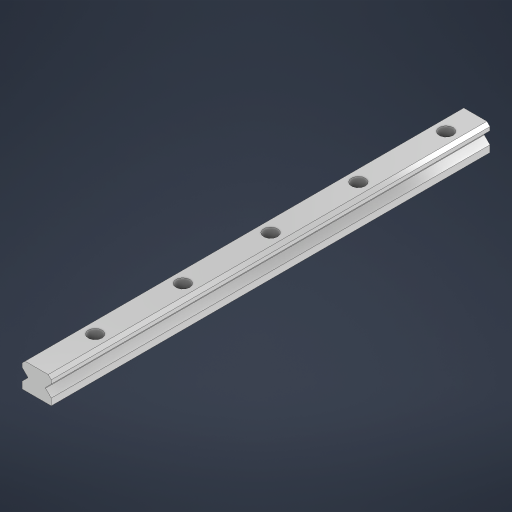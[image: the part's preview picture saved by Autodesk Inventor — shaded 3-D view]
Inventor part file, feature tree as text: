
AUTODESK INVENTOR PART (.ipt)
format: ipt  version: 2024.2 (Build 282272000, 272)  size: 227,840 bytes
history: native  units: mm
features: extrude x3, sketch x2, pattern_linear x1
ambient origin geometry x8: Origin, YZ Plane, XZ Plane, XY Plane, X Axis, Y Axis, Z Axis, Center Point
bodies: Solid1 (feature_tree)
feature tree (6):
  extrude  "Extrusion1"  Depth=20.0mm
  sketch  "Sketch2"  dims[d2=4.6mm d3=8.5mm d8=135.0deg d9=0.5mm d10=135.0deg d11=2.5mm d12=300.0mm d13=0.0mm d14=20.0mm d15=60.0mm d16=9.5mm d17=6.0mm d18=8.5mm d19=0.0mm d20=8.5mm d21=0.0mm d22=90.0mm d24=60.0mm]
  extrude  "Extrusion2"  Depth=8.5mm
  extrude  "Extrusion3"  TaperAngle=135.0deg  [1 undecoded]
  pattern_linear  "Rectangular Pattern1"  Spacing1=0.5mm  [1 undecoded]
  sketch  "Sketch1"  dims[d0=17.5mm d1=20.0mm]
note: 2 required parameter values undecoded (feature->parameter linkage not recoverable at this tier; creation-order binding heuristic only, values carry confidence <= 0.55)
